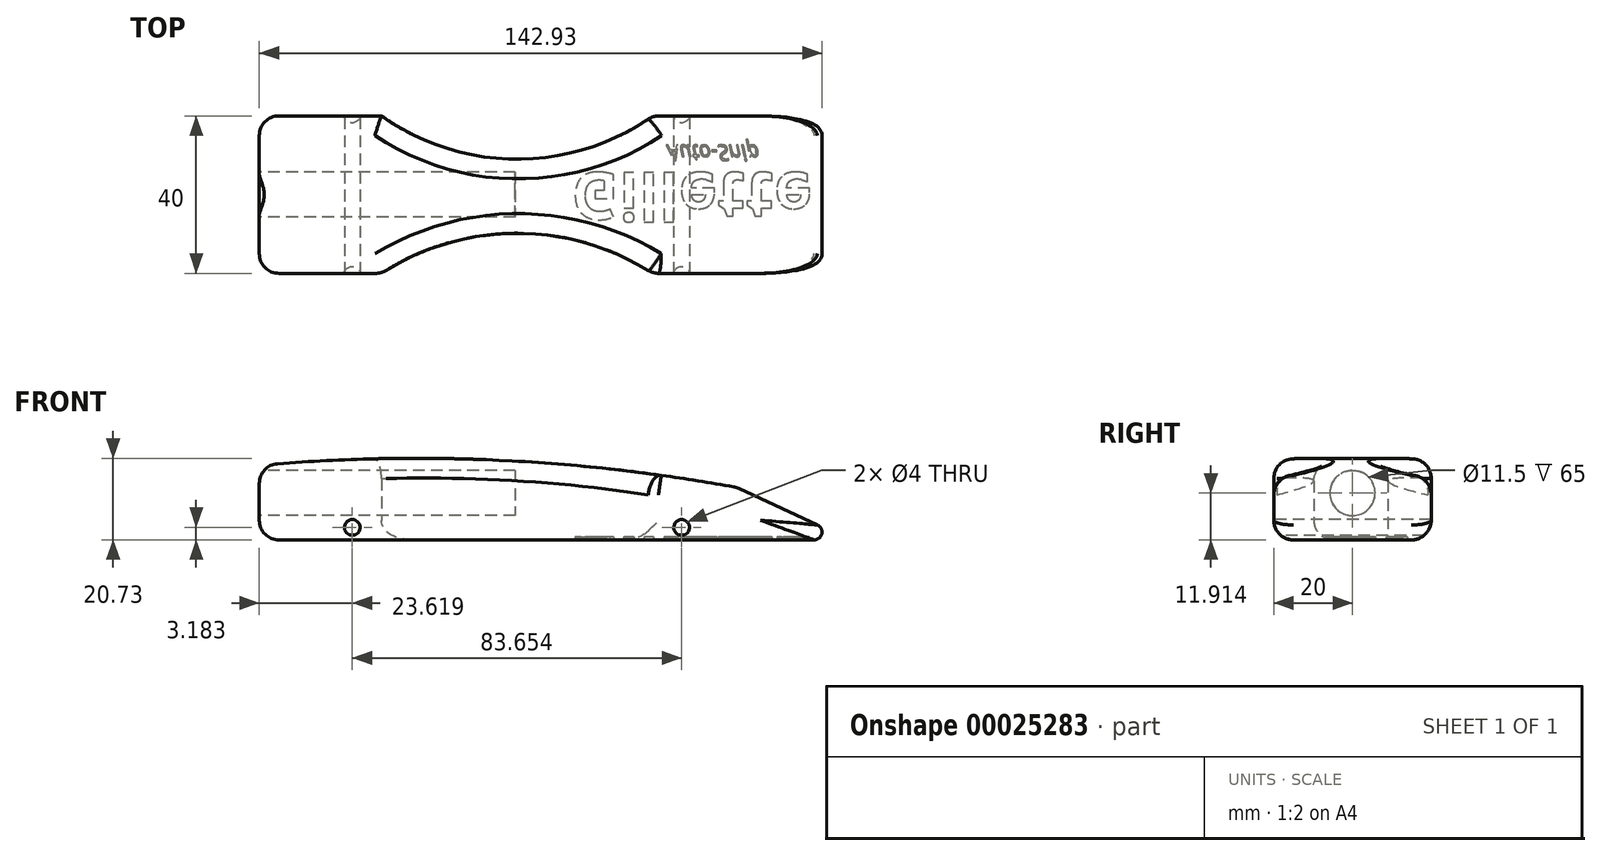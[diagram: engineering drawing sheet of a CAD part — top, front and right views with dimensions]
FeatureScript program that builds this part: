
annotation { "Feature Type Name" : "Feature", "Feature Type Description" : "" }
export const myFeature = defineFeature(function(context is Context, id is Id, definition is map)
    precondition{}
    {
        {
            var Q0;
            Q0=qCreatedBy(makeId("Front.planeOp"),FACE);
            var sketch = newSketch(context, id + "F0", { "sketchPlane" : qUnion([Q0])});
            skLineSegment(sketch, "E0.bottom", {"start": v(-84.2, -32.3) * mm, "end": v(65.8, -32.3) * mm});
            skLineSegment(sketch, "E0.top", {"start": v(-84.2, -2.3) * mm, "end": v(65.8, -2.3) * mm});
            skLineSegment(sketch, "E0.left", {"start": v(-84.2, -32.3) * mm, "end": v(-84.2, -2.3) * mm});
            skLineSegment(sketch, "E0.right", {"start": v(65.8, -32.3) * mm, "end": v(65.8, -2.3) * mm});
            skArc(sketch, "E1", {"start": v(65.8, -25.23) * mm, "mid": v(-8.7, -12.98) * mm, "end": v(-84.2, -13.33) * mm});
            skLineSegment(sketch, "E2", {"start": v(37.07, -18.98) * mm, "end": v(65.8, -32.3) * mm});
            skSolve(sketch);
        }
        {
            var Q0;
            Q0=makeQuery(id+"F0.imprint","IMPRINT",FACE,{"disambiguationData":[TD([[makeQuery(id+"F0.imprint","IMPRINT",EDGE,{"derivedFrom":sQuery(id+"F0.wireOp",EDGE,"E0.bottom")}),1.0]])]});
            extrude(context, id + "F1", {"entities" : qUnion([Q0]), "depth" : 40 * mm});
        }
        {
            var Q0;
            Q0=makeQuery(id+"F1.opExtrude","SWEPT_FACE",FACE,{"disambiguationData":[OSD([sQuery(id+"F0.wireOp",EDGE,"E0.left")])]});
            var sketch = newSketch(context, id + "F2", { "sketchPlane" : qUnion([Q0])});
            skPoint(sketch, "E3.orphan", {"position": v(20, -32.3) * mm});
            skCircle(sketch, "E4", {"center": v(20, -20.39) * mm, "radius": 5.75 * mm});
            skLineSegment(sketch, "E5", {"start": v(20, -13.33) * mm, "end": v(20, -34.42) * mm});
            skSolve(sketch);
        }
        {
            var Q0;
            Q0=makeQuery(id+"F2.imprint","IMPRINT",FACE,{"disambiguationData":[TD([[makeQuery(id+"F2.imprint","IMPRINT",EDGE,{"derivedFrom":sQuery(id+"F2.wireOp",EDGE,"434b94d7-23d6-471c-86e1-b71db2b08216")}),1.0]])]});
            var Q1;
            Q1=makeQuery(id+"F2.imprint","IMPRINT",FACE,{"disambiguationData":[TD([[makeQuery(id+"F2.imprint","IMPRINT",EDGE,{"derivedFrom":sQuery(id+"F2.wireOp",EDGE,"E4")}),1.0]])]});
            extrude(context, id + "F3", {"entities" : qUnion([Q0, Q1]), "operationType" : NewBodyOperationType.REMOVE, "oppositeDirection" : true, "depth" : 65 * mm});
        }
        {
            var Q0;
            Q0=makeQuery(id+"F1.opExtrude","CAP_FACE",FACE,{"disambiguationData":[OSD([sQuery(id+"F0.wireOp",EDGE,"E0.bottom"),sQuery(id+"F0.wireOp",EDGE,"E0.top"),sQuery(id+"F0.wireOp",EDGE,"E0.left"),sQuery(id+"F0.wireOp",EDGE,"E0.right")])],"isStart":false});
            var sketch = newSketch(context, id + "F4", { "sketchPlane" : qUnion([Q0])});
            skCircle(sketch, "E6", {"center": v(-60.58, -29.12) * mm, "radius": 2 * mm});
            skCircle(sketch, "E7", {"center": v(23.07, -29.12) * mm, "radius": 2 * mm});
            skSolve(sketch);
        }
        {
            var Q0;
            Q0=makeQuery(id+"F4.imprint","IMPRINT",FACE,{"disambiguationData":[TD([[makeQuery(id+"F4.imprint","IMPRINT",EDGE,{"derivedFrom":sQuery(id+"F4.wireOp",EDGE,"E6")}),1.0]])]});
            var Q1;
            Q1=makeQuery(id+"F4.imprint","IMPRINT",FACE,{"disambiguationData":[TD([[makeQuery(id+"F4.imprint","IMPRINT",EDGE,{"derivedFrom":sQuery(id+"F4.wireOp",EDGE,"E7")}),1.0]])]});
            var Q2;
            {var subQ1=sQuery(id+"F4.wireOp",EDGE,"a27f094f-d759-46df-924c-4756f3068108");Q2=makeQuery(id+"F4.imprint","IMPRINT",FACE,{"disambiguationData":[TD([[makeQuery(id+"F4.imprint","IMPRINT",EDGE,{"derivedFrom":subQ1}),1.0]])]});}
            var Q3;
            {var subQ1=sQuery(id+"F4.wireOp",EDGE,"a6277ecb-bbd8-4e38-8477-1489fa49aca8");Q3=makeQuery(id+"F4.imprint","IMPRINT",FACE,{"disambiguationData":[TD([[makeQuery(id+"F4.imprint","IMPRINT",EDGE,{"derivedFrom":subQ1}),1.0]])]});}
            extrude(context, id + "F5", {"entities" : qUnion([Q0, Q1, Q2, Q3]), "operationType" : NewBodyOperationType.REMOVE, "endBound" : BoundingType.THROUGH_ALL, "oppositeDirection" : true, "depth" : 25 * mm});
        }
        {
            var Q0;
            Q0=makeQuery(id+"F1.opExtrude","SWEPT_FACE",FACE,{"disambiguationData":[OSD([sQuery(id+"F0.wireOp",EDGE,"E0.bottom")])]});
            var sketch = newSketch(context, id + "F6", { "sketchPlane" : qUnion([Q0])});
            skArc(sketch, "E8", {"start": v(15.77, 0) * mm, "mid": v(-18.7, 11) * mm, "end": v(-53.16, 0) * mm});
            skArc(sketch, "E9", {"start": v(-53.16, 40) * mm, "mid": v(-18.7, 29.82) * mm, "end": v(15.77, 40) * mm});
            skSolve(sketch);
        }
        {
            var Q0;
            Q0 = qSketchRegion(id + "F6", true);
            var Q1;
            {var subQ1=sQuery(id+"F6.wireOp",EDGE,"E8");Q1=makeQuery(id+"F6.imprint","IMPRINT",FACE,{"disambiguationData":[TD([[makeQuery(id+"F6.imprint","IMPRINT",EDGE,{"derivedFrom":subQ1}),1.0]])]});}
            var Q2;
            {var subQ1=sQuery(id+"F6.wireOp",EDGE,"E9");Q2=makeQuery(id+"F6.imprint","IMPRINT",FACE,{"disambiguationData":[TD([[makeQuery(id+"F6.imprint","IMPRINT",EDGE,{"derivedFrom":subQ1}),1.0]])]});}
            extrude(context, id + "F7", {"entities" : qUnion([Q0, Q1, Q2]), "operationType" : NewBodyOperationType.REMOVE, "endBound" : BoundingType.THROUGH_ALL, "oppositeDirection" : true, "depth" : 25 * mm});
        }
        {
            var Q0;
            Q0=makeQuery(id+"F7.boolean.opBoolean","COPY",FACE,{"derivedFrom":makeQuery(id+"F7.opExtrude","SWEPT_FACE",FACE,{"disambiguationData":[OSD([sQuery(id+"F6.wireOp",EDGE,"E9")])]})});
            var Q1;
            {var subQ0=sQuery(id+"F0.wireOp",EDGE,"E1");var subQ1=sQuery(id+"F0.wireOp",EDGE,"E0.left");Q1=makeQuery(id+"F7.boolean.opBoolean","SPLIT",EDGE,{"disambiguationData":[TD([makeQuery(id+"F1.opExtrude","SWEPT_FACE",FACE,{"disambiguationData":[OSD([subQ1])]})])],"derivedFrom":makeQuery(id+"F1.opExtrude","CAP_EDGE",EDGE,{"disambiguationData":[OSD([subQ0])],"isStart":false})});}
            var Q2;
            {var subQ0=sQuery(id+"F0.wireOp",EDGE,"E0.bottom");var subQ1=sQuery(id+"F0.wireOp",EDGE,"E0.left");Q2=makeQuery(id+"F7.boolean.opBoolean","SPLIT",EDGE,{"disambiguationData":[TD([makeQuery(id+"F1.opExtrude","SWEPT_FACE",FACE,{"disambiguationData":[OSD([subQ1])]})])],"derivedFrom":makeQuery(id+"F1.opExtrude","CAP_EDGE",EDGE,{"disambiguationData":[OSD([subQ0])],"isStart":false})});}
            var Q3;
            Q3=makeQuery(id+"F1.opExtrude","SWEPT_EDGE",EDGE,{"disambiguationData":[OSD([sQuery(id+"F0.wireOp",EDGE,"E0.left"),sQuery(id+"F0.wireOp",EDGE,"E1")])]});
            var Q4;
            Q4=makeQuery(id+"F1.opExtrude","CAP_EDGE",EDGE,{"disambiguationData":[OSD([sQuery(id+"F0.wireOp",EDGE,"E0.left")])],"isStart":false});
            var Q5;
            Q5=makeQuery(id+"F1.opExtrude","SWEPT_EDGE",EDGE,{"disambiguationData":[OSD([sQuery(id+"F0.wireOp",EDGE,"E0.bottom"),sQuery(id+"F0.wireOp",EDGE,"E0.left")])]});
            var Q6;
            {var subQ0=sQuery(id+"F0.wireOp",EDGE,"E0.bottom");var subQ1=sQuery(id+"F0.wireOp",EDGE,"E0.left");Q6=makeQuery(id+"F7.boolean.opBoolean","SPLIT",EDGE,{"disambiguationData":[TD([makeQuery(id+"F1.opExtrude","SWEPT_FACE",FACE,{"disambiguationData":[OSD([subQ1])]})])],"derivedFrom":makeQuery(id+"F1.opExtrude","CAP_EDGE",EDGE,{"disambiguationData":[OSD([subQ0])],"isStart":true})});}
            var Q7;
            {var subQ0=sQuery(id+"F0.wireOp",EDGE,"E1");var subQ1=sQuery(id+"F0.wireOp",EDGE,"E0.left");Q7=makeQuery(id+"F7.boolean.opBoolean","SPLIT",EDGE,{"disambiguationData":[TD([makeQuery(id+"F1.opExtrude","SWEPT_FACE",FACE,{"disambiguationData":[OSD([subQ1])]})])],"derivedFrom":makeQuery(id+"F1.opExtrude","CAP_EDGE",EDGE,{"disambiguationData":[OSD([subQ0])],"isStart":true})});}
            var Q8;
            Q8=makeQuery(id+"F1.opExtrude","CAP_EDGE",EDGE,{"disambiguationData":[OSD([sQuery(id+"F0.wireOp",EDGE,"E0.left")])],"isStart":true});
            var Q9;
            Q9=makeQuery(id+"F7.boolean.opBoolean","INTERSECT",EDGE,{"derivedFrom":[makeQuery(id+"F1.opExtrude","SWEPT_FACE",FACE,{"disambiguationData":[OSD([sQuery(id+"F0.wireOp",EDGE,"E1")])]}),makeQuery(id+"F7.opExtrude","SWEPT_FACE",FACE,{"disambiguationData":[OSD([sQuery(id+"F6.wireOp",EDGE,"E8")])]})]});
            var Q10;
            Q10=makeQuery(id+"F7.boolean.opBoolean","COPY",EDGE,{"derivedFrom":makeQuery(id+"F7.opExtrude","CAP_EDGE",EDGE,{"disambiguationData":[OSD([sQuery(id+"F6.wireOp",EDGE,"E8")])],"isStart":true})});
            fillet(context, id + "F8", {"entities" : qUnion([Q0, Q1, Q2, Q3, Q4, Q5, Q6, Q7, Q8, Q9, Q10]), "radius" : 5 * mm, "tangentPropagation" : true, "allowEdgeOverflow" : false});
        }
        {
            var Q0;
            Q0=makeQuery(id+"F1.opExtrude","SWEPT_EDGE",EDGE,{"disambiguationData":[OSD([sQuery(id+"F0.wireOp",EDGE,"E0.bottom"),sQuery(id+"F0.wireOp",EDGE,"E0.right"),sQuery(id+"F0.wireOp",EDGE,"E2")])]});
            fillet(context, id + "F9", {"entities" : qUnion([Q0]), "radius" : 2 * mm, "tangentPropagation" : true, "allowEdgeOverflow" : false});
        }
        {
            var Q0;
            Q0=makeQuery(id+"F1.opExtrude","SWEPT_FACE",FACE,{"disambiguationData":[OSD([sQuery(id+"F0.wireOp",EDGE,"E0.bottom")])]});
            var sketch = newSketch(context, id + "F10", { "sketchPlane" : qUnion([Q0])});
            skText(sketch, "E10", { "text": "Gillette", "fontName": "OpenSans-Bold.ttf"});
            skText(sketch, "E11", { "text": "Auto-Snip", "fontName": "OpenSans-Italic.ttf"});
            const initialGuessF10  = {"E10": [-0.00489, 0.0144, 1, 0, 0.01195], "E11": [0.0194, 0.0074, 1, 0, 0.00397]};
            skSetInitialGuess(sketch, initialGuessF10);
            skSolve(sketch);
        }
        {
            var Q0;
            Q0 = qSketchRegion(id + "F10", true);
            extrude(context, id + "F11", {"entities" : qUnion([Q0]), "operationType" : NewBodyOperationType.REMOVE, "oppositeDirection" : true, "depth" : 0.7 * mm});
        }
        {
            var Q0;
            Q0=makeQuery(id+"F1.opExtrude","SWEPT_FACE",FACE,{"disambiguationData":[OSD([sQuery(id+"F0.wireOp",EDGE,"E1")])]});
            var Q1;
            Q1=makeQuery(id+"F1.opExtrude","SWEPT_FACE",FACE,{"disambiguationData":[OSD([sQuery(id+"F0.wireOp",EDGE,"E2")])]});
            fillet(context, id + "F12", {"entities" : qUnion([Q0, Q1]), "radius" : 5 * mm, "tangentPropagation" : true, "allowEdgeOverflow" : false});
        }
    });
